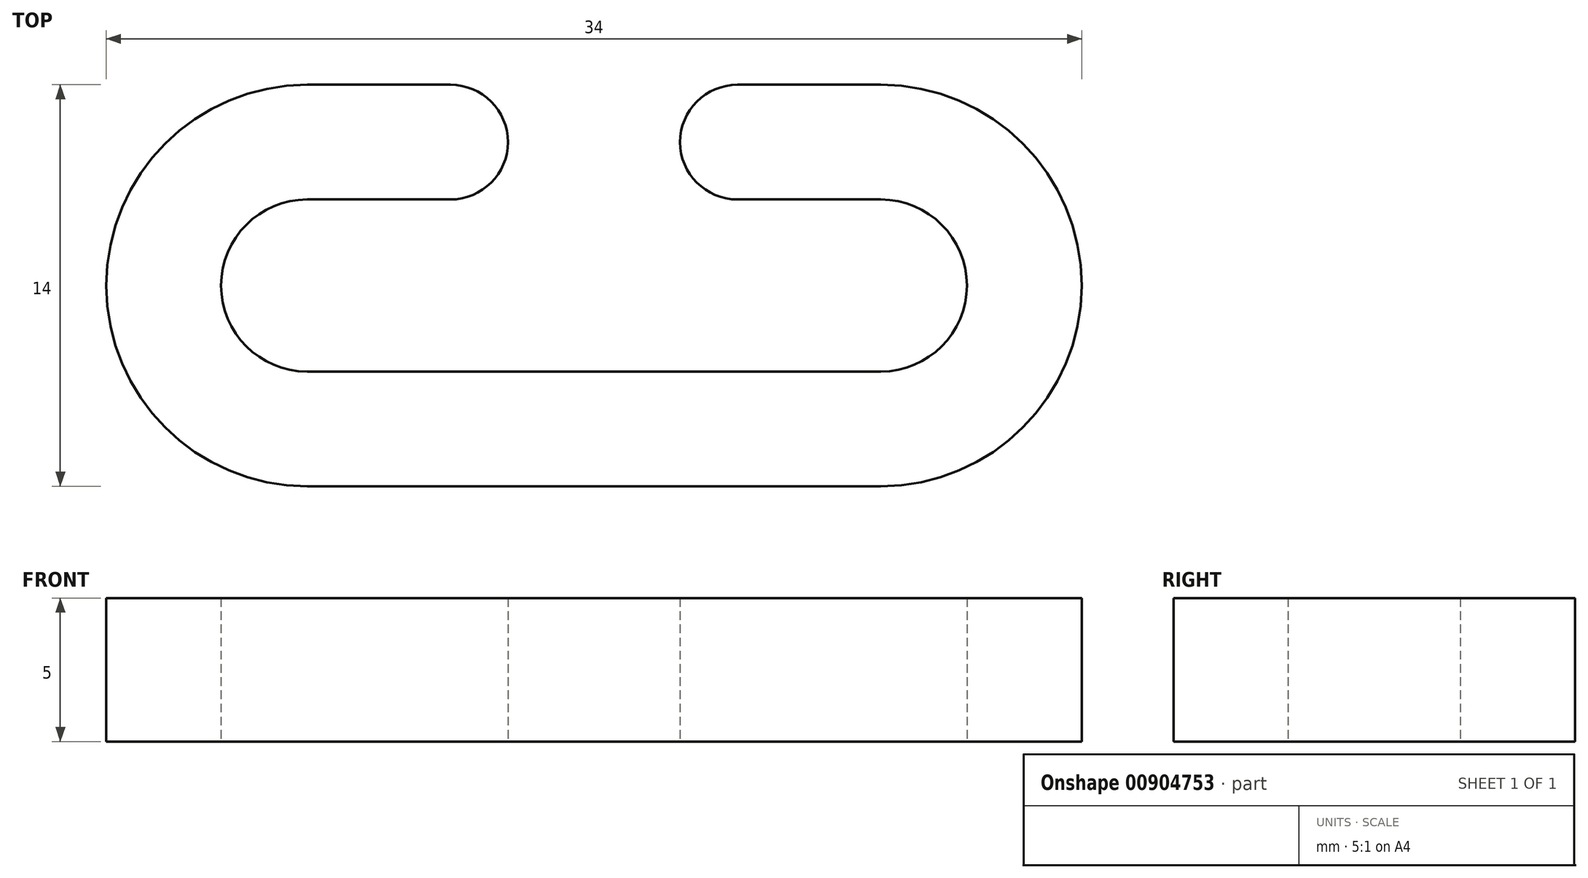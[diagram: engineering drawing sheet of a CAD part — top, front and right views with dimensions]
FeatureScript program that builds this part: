
annotation { "Feature Type Name" : "Feature", "Feature Type Description" : "" }
export const myFeature = defineFeature(function(context is Context, id is Id, definition is map)
    precondition{}
    {
        {
            var Q0;
            Q0=qCreatedBy(makeId("Top.planeOp"),FACE);
            var sketch = newSketch(context, id + "F0", { "sketchPlane" : qUnion([Q0])});
            skLineSegment(sketch, "E0", {"start": v(-10, 0) * mm, "end": v(10, 0) * mm, "construction": true});
            skArc(sketch, "E1.0.startCap", {"start": v(-10, -3) * mm, "mid": v(-13, 0) * mm, "end": v(-10, 3) * mm});
            skArc(sketch, "E1.0.endCap", {"start": v(10, 3) * mm, "mid": v(13, 0) * mm, "end": v(10, -3) * mm});
            skLineSegment(sketch, "E1.0.left", {"start": v(-10, 3) * mm, "end": v(-5, 3) * mm});
            skLineSegment(sketch, "E1.0.right", {"start": v(-10, -3) * mm, "end": v(10, -3) * mm});
            skArc(sketch, "E2.0.startCap", {"start": v(-10, -7) * mm, "mid": v(-17, 0) * mm, "end": v(-10, 7) * mm});
            skArc(sketch, "E2.0.endCap", {"start": v(10, 7) * mm, "mid": v(17, 0) * mm, "end": v(10, -7) * mm});
            skLineSegment(sketch, "E2.0.left", {"start": v(-10, 7) * mm, "end": v(-5, 7) * mm});
            skLineSegment(sketch, "E2.0.right", {"start": v(-10, -7) * mm, "end": v(10, -7) * mm});
            skLineSegment(sketch, "E3.trimOffspring", {"start": v(5, 7) * mm, "end": v(10, 7) * mm});
            skLineSegment(sketch, "E4.trimOffspring", {"start": v(5, 3) * mm, "end": v(10, 3) * mm});
            skArc(sketch, "E5", {"start": v(-5, 3) * mm, "mid": v(-3, 5) * mm, "end": v(-5, 7) * mm});
            skArc(sketch, "E6", {"start": v(5, 7) * mm, "mid": v(3, 5) * mm, "end": v(5, 3) * mm});
            skSolve(sketch);
        }
        {
            var Q0;
            Q0 = qSketchRegion(id + "F0", true);
            extrude(context, id + "F1", {"entities" : qUnion([Q0]), "depth" : 5 * mm, "offsetDistance" : 25 * mm});
        }
    });
